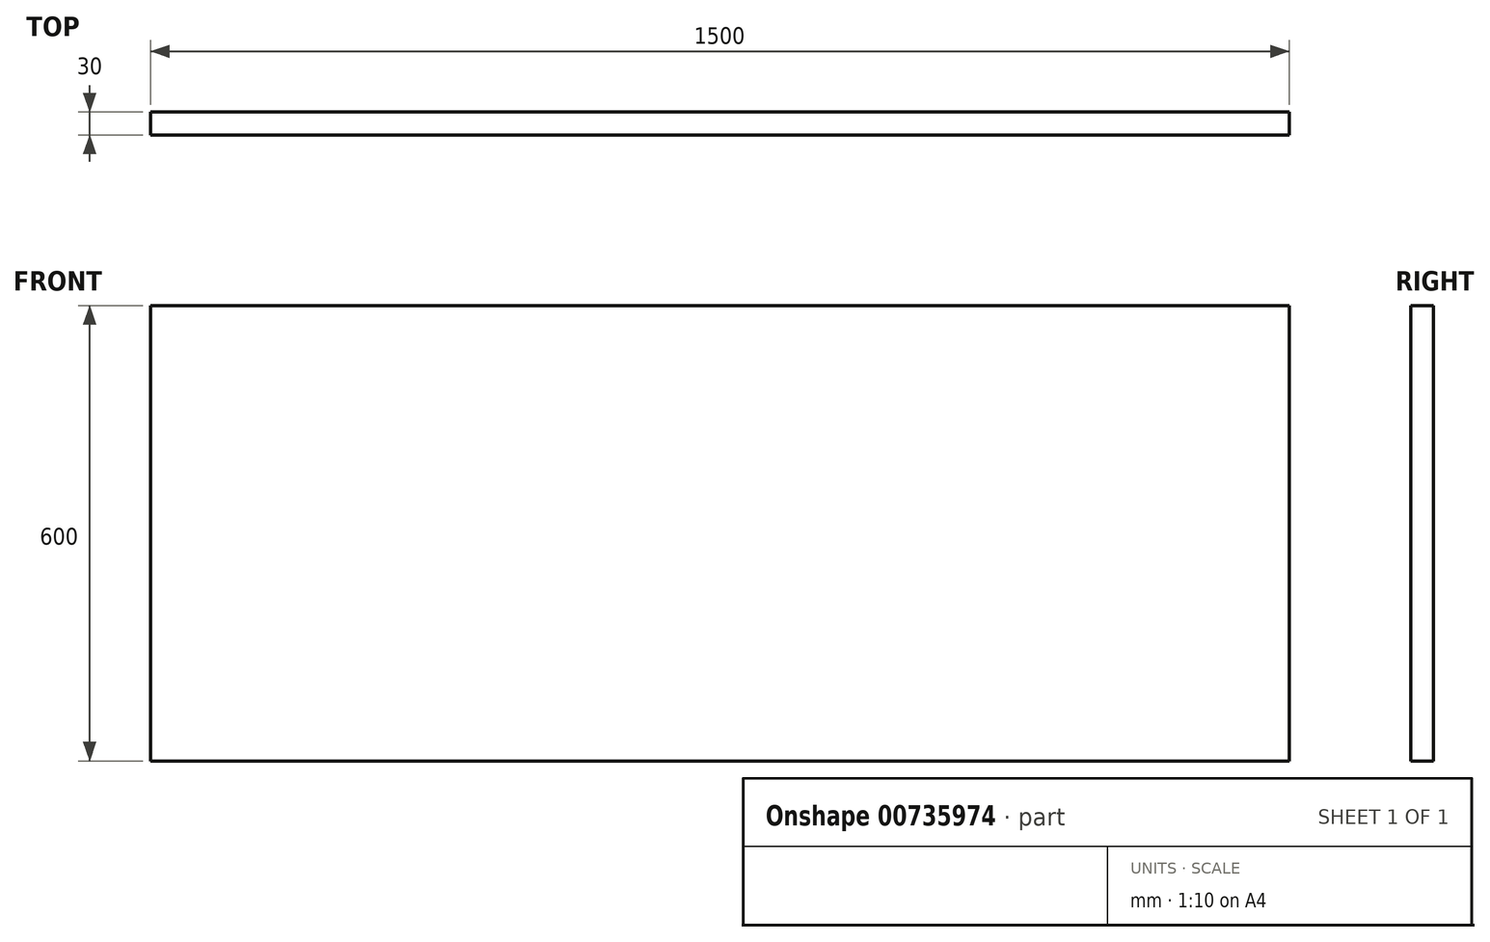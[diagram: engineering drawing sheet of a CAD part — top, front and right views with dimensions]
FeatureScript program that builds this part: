
annotation { "Feature Type Name" : "Feature", "Feature Type Description" : "" }
export const myFeature = defineFeature(function(context is Context, id is Id, definition is map)
    precondition{}
    {
        {
            var Q0;
            Q0=qCreatedBy(makeId("Front.planeOp"),FACE);
            var sketch = newSketch(context, id + "F0", { "sketchPlane" : qUnion([Q0])});
            skLineSegment(sketch, "E0.bottom", {"start": v(750, -300) * mm, "end": v(-750, -300) * mm});
            skLineSegment(sketch, "E0.top", {"start": v(750, 300) * mm, "end": v(-750, 300) * mm});
            skLineSegment(sketch, "E0.left", {"start": v(750, -300) * mm, "end": v(750, 300) * mm});
            skLineSegment(sketch, "E0.right", {"start": v(-750, -300) * mm, "end": v(-750, 300) * mm});
            skPoint(sketch, "E0.middle", {"position": v(0, 0) * mm});
            skSolve(sketch);
        }
        {
            var Q0;
            Q0 = qSketchRegion(id + "F0", true);
            extrude(context, id + "F1", {"entities" : qUnion([Q0]), "endBound" : BoundingType.SYMMETRIC, "depth" : 30 * mm, "offsetDistance" : 25 * mm});
        }
    });
